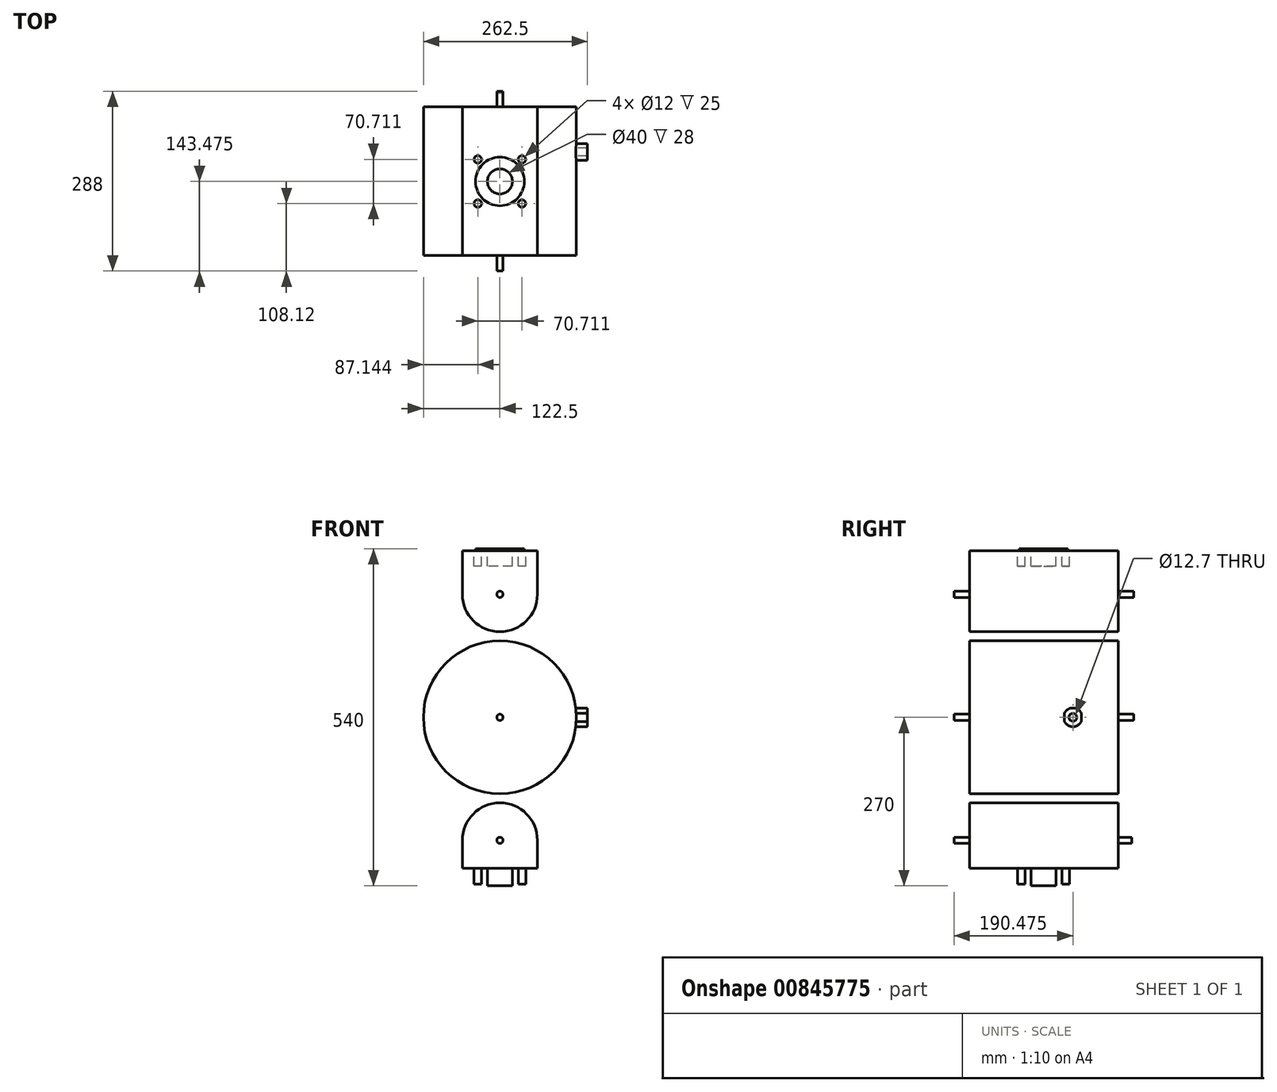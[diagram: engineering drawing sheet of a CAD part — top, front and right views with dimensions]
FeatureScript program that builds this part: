
annotation { "Feature Type Name" : "Feature", "Feature Type Description" : "" }
export const myFeature = defineFeature(function(context is Context, id is Id, definition is map)
    precondition{}
    {
        {
            var Q0;
            Q0=qCreatedBy(makeId("Front.planeOp"),FACE);
            var sketch = newSketch(context, id + "F0", { "sketchPlane" : qUnion([Q0])});
            skCircle(sketch, "E0", {"center": v(0, 0) * mm, "radius": 122.5 * mm});
            skSolve(sketch);
        }
        {
            var Q0;
            Q0=makeQuery(id+"F0.imprint","IMPRINT",FACE,{"disambiguationData":[TD([[makeQuery(id+"F0.imprint","IMPRINT",EDGE,{"derivedFrom":sQuery(id+"F0.wireOp",EDGE,"E0")}),1.0]])]});
            var sketch = newSketch(context, id + "F1", { "sketchPlane" : qUnion([Q0])});
            skArc(sketch, "E1", {"start": v(-60, 197) * mm, "mid": v(0, 137) * mm, "end": v(60, 197) * mm});
            skLineSegment(sketch, "E2.bottom", {"start": v(60, 267) * mm, "end": v(-60, 267) * mm});
            skLineSegment(sketch, "E2.left", {"start": v(60, 267) * mm, "end": v(60, 197) * mm});
            skLineSegment(sketch, "E2.right", {"start": v(-60, 267) * mm, "end": v(-60, 197) * mm});
            skArc(sketch, "E3.MirrorCS", {"start": v(-60, -197) * mm, "mid": v(0, -137) * mm, "end": v(60, -197) * mm});
            skLineSegment(sketch, "E4.MirrorCS", {"start": v(60, -267) * mm, "end": v(-60, -267) * mm});
            skLineSegment(sketch, "E5.MirrorCS", {"start": v(-60, -267) * mm, "end": v(-60, -197) * mm});
            skLineSegment(sketch, "E6.MirrorCS", {"start": v(60, -267) * mm, "end": v(60, -197) * mm});
            skSolve(sketch);
        }
        {
            var Q0;
            Q0 = qSketchRegion(id + "F1", true);
            var Q1;
            Q1 = qSketchRegion(id + "F0", true);
            extrude(context, id + "F2", {"entities" : qUnion([Q0, Q1]), "depth" : 238 * mm, "offsetDistance" : 25 * mm});
        }
        {
            var Q0;
            Q0=makeQuery(id+"F2.opExtrude","CAP_FACE",FACE,{"disambiguationData":[OSD([sQuery(id+"F0.wireOp",EDGE,"E0")])],"isStart":false});
            var sketch = newSketch(context, id + "F3", { "sketchPlane" : qUnion([Q0])});
            skCircle(sketch, "E7", {"center": v(0, 0) * mm, "radius": 5 * mm});
            skCircle(sketch, "E8", {"center": v(0, 197) * mm, "radius": 5 * mm});
            skCircle(sketch, "E9", {"center": v(0, -197) * mm, "radius": 5 * mm});
            skSolve(sketch);
        }
        {
            var Q0;
            Q0=makeQuery(id+"F3.imprint","IMPRINT",FACE,{"disambiguationData":[TD([[makeQuery(id+"F3.imprint","IMPRINT",EDGE,{"derivedFrom":sQuery(id+"F3.wireOp",EDGE,"E8")}),1.0]])]});
            extrude(context, id + "F4", {"entities" : qUnion([Q0]), "operationType" : NewBodyOperationType.ADD, "depth" : 25 * mm, "offsetDistance" : 25 * mm, "hasSecondDirection" : true, "secondDirectionOppositeDirection" : true, "secondDirectionDepth" : (238 + 25) * mm});
        }
        {
            var Q0;
            Q0=makeQuery(id+"F3.imprint","IMPRINT",FACE,{"disambiguationData":[TD([[makeQuery(id+"F3.imprint","IMPRINT",EDGE,{"derivedFrom":sQuery(id+"F3.wireOp",EDGE,"E7")}),1.0]])]});
            var Q1;
            Q1=sQuery(id+"F3.wireOp",EDGE,"E7");
            extrude(context, id + "F5", {"entities" : qUnion([Q0]), "operationType" : NewBodyOperationType.ADD, "surfaceOperationType" : NewSurfaceOperationType.ADD, "surfaceEntities" : qUnion([Q1]), "depth" : 25 * mm, "offsetDistance" : 25 * mm, "hasSecondDirection" : true, "secondDirectionOppositeDirection" : true, "secondDirectionDepth" : (238 + 25) * mm});
        }
        {
            var Q0;
            Q0=makeQuery(id+"F3.imprint","IMPRINT",FACE,{"disambiguationData":[TD([[makeQuery(id+"F3.imprint","IMPRINT",EDGE,{"derivedFrom":sQuery(id+"F3.wireOp",EDGE,"E9")}),1.0]])]});
            var Q1;
            Q1=sQuery(id+"F3.wireOp",EDGE,"E9");
            extrude(context, id + "F6", {"entities" : qUnion([Q0]), "operationType" : NewBodyOperationType.ADD, "surfaceEntities" : qUnion([Q1]), "depth" : 25 * mm, "offsetDistance" : 25 * mm, "hasSecondDirection" : true, "secondDirectionOppositeDirection" : true, "secondDirectionDepth" : (25 + 235) * mm});
        }
        {
            var Q0;
            Q0=makeQuery(id+"F2.opExtrude","SWEPT_FACE",FACE,{"disambiguationData":[OSD([sQuery(id+"F1.wireOp",EDGE,"E2.bottom")])]});
            var sketch = newSketch(context, id + "F7", { "sketchPlane" : qUnion([Q0])});
            skCircle(sketch, "E10", {"center": v(0, -119.52) * mm, "radius": 20 * mm});
            skCircle(sketch, "E11", {"center": v(-35.36, -84.17) * mm, "radius": 6 * mm});
            skCircle(sketch, "E12.1.0", {"center": v(-35.35, -154.88) * mm, "radius": 6 * mm});
            skCircle(sketch, "E12.2.0", {"center": v(35.36, -154.88) * mm, "radius": 6 * mm});
            skCircle(sketch, "E12.3.0", {"center": v(35.35, -84.17) * mm, "radius": 6 * mm});
            skCircle(sketch, "E13", {"center": v(0, -119.52) * mm, "radius": 39 * mm});
            skSolve(sketch);
        }
        {
            var Q0;
            Q0=makeQuery(id+"F7.imprint","IMPRINT",FACE,{"disambiguationData":[TD([[makeQuery(id+"F7.imprint","IMPRINT",EDGE,{"derivedFrom":sQuery(id+"F7.wireOp",EDGE,"E10")}),1.0]])]});
            var Q1;
            Q1=makeQuery(id+"F7.imprint","IMPRINT",FACE,{"disambiguationData":[TD([[makeQuery(id+"F7.imprint","IMPRINT",EDGE,{"derivedFrom":sQuery(id+"F7.wireOp",EDGE,"E12.1.0")}),1.0]])]});
            var Q2;
            Q2=makeQuery(id+"F7.imprint","IMPRINT",FACE,{"disambiguationData":[TD([[makeQuery(id+"F7.imprint","IMPRINT",EDGE,{"derivedFrom":sQuery(id+"F7.wireOp",EDGE,"E12.2.0")}),1.0]])]});
            var Q3;
            Q3=makeQuery(id+"F7.imprint","IMPRINT",FACE,{"disambiguationData":[TD([[makeQuery(id+"F7.imprint","IMPRINT",EDGE,{"derivedFrom":sQuery(id+"F7.wireOp",EDGE,"E12.3.0")}),1.0]])]});
            var Q4;
            Q4=makeQuery(id+"F7.imprint","IMPRINT",FACE,{"disambiguationData":[TD([[makeQuery(id+"F7.imprint","IMPRINT",EDGE,{"derivedFrom":sQuery(id+"F7.wireOp",EDGE,"E11")}),1.0]])]});
            extrude(context, id + "F8", {"entities" : qUnion([Q0, Q1, Q2, Q3, Q4]), "operationType" : NewBodyOperationType.REMOVE, "oppositeDirection" : true, "depth" : 25 * mm, "offsetDistance" : 25 * mm});
        }
        {
            var Q0;
            Q0=makeQuery(id+"F7.imprint","IMPRINT",FACE,{"disambiguationData":[TD([[makeQuery(id+"F7.imprint","IMPRINT",EDGE,{"derivedFrom":sQuery(id+"F7.wireOp",EDGE,"E10")}),-1.0]])]});
            extrude(context, id + "F9", {"entities" : qUnion([Q0]), "operationType" : NewBodyOperationType.ADD, "depth" : 3 * mm, "offsetDistance" : 25 * mm});
        }
        {
            var Q0;
            Q0=makeQuery(id+"F2.opExtrude","SWEPT_FACE",FACE,{"disambiguationData":[OSD([sQuery(id+"F1.wireOp",EDGE,"E4.MirrorCS")])]});
            var sketch = newSketch(context, id + "F10", { "sketchPlane" : qUnion([Q0])});
            skCircle(sketch, "E14.0", {"center": v(0, 119.52) * mm, "radius": 20 * mm});
            skCircle(sketch, "E15.0", {"center": v(0, 119.52) * mm, "radius": 39 * mm});
            skCircle(sketch, "E16.0", {"center": v(35.36, 154.88) * mm, "radius": 6 * mm});
            skCircle(sketch, "E17.0", {"center": v(35.35, 84.17) * mm, "radius": 6 * mm});
            skCircle(sketch, "E18.0", {"center": v(-35.36, 154.88) * mm, "radius": 6 * mm});
            skCircle(sketch, "E19.0", {"center": v(-35.36, 84.17) * mm, "radius": 6 * mm});
            skSolve(sketch);
        }
        {
            var Q0;
            Q0=makeQuery(id+"F10.imprint","IMPRINT",FACE,{"disambiguationData":[TD([[makeQuery(id+"F10.imprint","IMPRINT",EDGE,{"derivedFrom":sQuery(id+"F10.wireOp",EDGE,"E14.0")}),-1.0]])]});
            var Q1;
            Q1=makeQuery(id+"F10.imprint","IMPRINT",FACE,{"disambiguationData":[TD([[makeQuery(id+"F10.imprint","IMPRINT",EDGE,{"derivedFrom":sQuery(id+"F10.wireOp",EDGE,"E16.0")}),-1.0]])]});
            var Q2;
            Q2=makeQuery(id+"F10.imprint","IMPRINT",FACE,{"disambiguationData":[TD([[makeQuery(id+"F10.imprint","IMPRINT",EDGE,{"derivedFrom":sQuery(id+"F10.wireOp",EDGE,"E17.0")}),-1.0]])]});
            var Q3;
            Q3=makeQuery(id+"F10.imprint","IMPRINT",FACE,{"disambiguationData":[TD([[makeQuery(id+"F10.imprint","IMPRINT",EDGE,{"derivedFrom":sQuery(id+"F10.wireOp",EDGE,"E18.0")}),-1.0]])]});
            var Q4;
            Q4=makeQuery(id+"F10.imprint","IMPRINT",FACE,{"disambiguationData":[TD([[makeQuery(id+"F10.imprint","IMPRINT",EDGE,{"derivedFrom":sQuery(id+"F10.wireOp",EDGE,"E19.0")}),-1.0]])]});
            extrude(context, id + "F11", {"entities" : qUnion([Q0, Q1, Q2, Q3, Q4]), "operationType" : NewBodyOperationType.REMOVE, "oppositeDirection" : true, "depth" : 25 * mm, "offsetDistance" : 25 * mm});
        }
        {
            var Q0;
            Q0=makeQuery(id+"F10.imprint","IMPRINT",FACE,{"disambiguationData":[TD([[makeQuery(id+"F10.imprint","IMPRINT",EDGE,{"derivedFrom":sQuery(id+"F10.wireOp",EDGE,"E14.0")}),1.0]])]});
            extrude(context, id + "F12", {"entities" : qUnion([Q0]), "operationType" : NewBodyOperationType.ADD, "depth" : 3 * mm, "offsetDistance" : 25 * mm});
        }
        {
            var Q0;
            Q0=qCreatedBy(makeId("Right.planeOp"),FACE);
            var sketch = newSketch(context, id + "F13", { "sketchPlane" : qUnion([Q0])});
            skCircle(sketch, "E20", {"center": v(-72.52, 0) * mm, "radius": 6.35 * mm});
            skArc(sketch, "E21", {"start": v(-86, -6.6) * mm, "mid": v(-72.52, -15) * mm, "end": v(-59.05, -6.6) * mm});
            skLineSegment(sketch, "E22.left", {"start": v(-86, 6.6) * mm, "end": v(-86, -6.6) * mm});
            skLineSegment(sketch, "E22.right", {"start": v(-59.05, 6.6) * mm, "end": v(-59.05, -6.6) * mm});
            skArc(sketch, "E23.trimOffspring", {"start": v(-59.05, 6.6) * mm, "mid": v(-72.52, 15) * mm, "end": v(-86, 6.6) * mm});
            skSolve(sketch);
        }
        {
            var Q0;
            Q0 = qSketchRegion(id + "F13", true);
            extrude(context, id + "F14", {"entities" : qUnion([Q0]), "operationType" : NewBodyOperationType.ADD, "depth" : 140 * mm, "offsetDistance" : 25 * mm});
        }
    });
